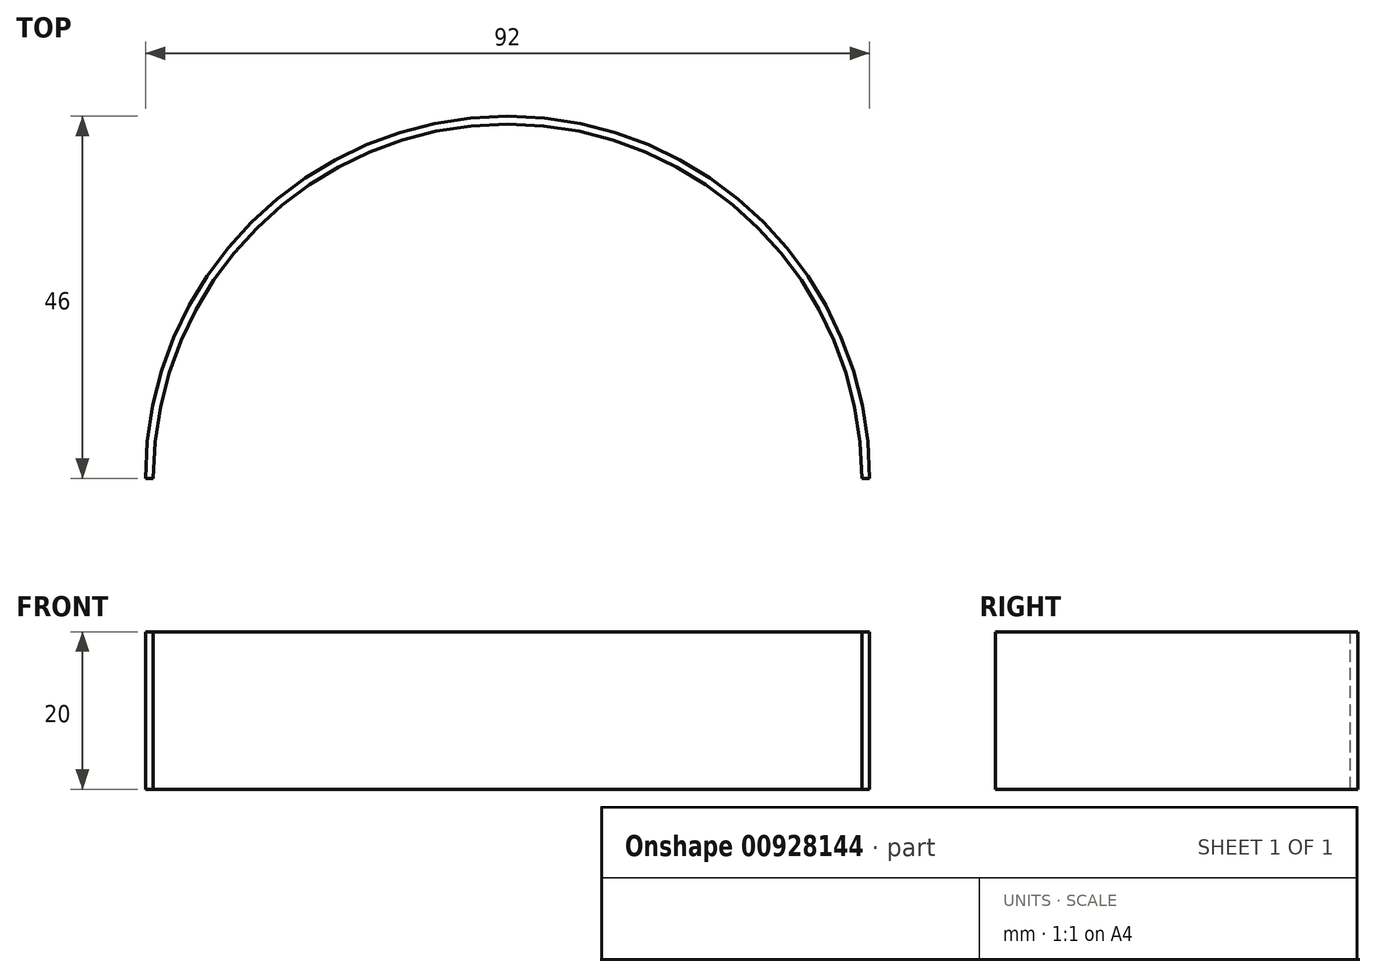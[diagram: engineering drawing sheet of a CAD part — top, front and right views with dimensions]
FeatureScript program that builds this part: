
annotation { "Feature Type Name" : "Feature", "Feature Type Description" : "" }
export const myFeature = defineFeature(function(context is Context, id is Id, definition is map)
    precondition{}
    {
        {
            var Q0;
            Q0=qCreatedBy(makeId("Top.planeOp"),FACE);
            var sketch = newSketch(context, id + "F0", { "sketchPlane" : qUnion([Q0])});
            skCircle(sketch, "E0", {"center": v(0, 0) * mm, "radius": 45 * mm});
            skCircle(sketch, "E1", {"center": v(0, 0) * mm, "radius": 46 * mm});
            skLineSegment(sketch, "E2", {"start": v(-64.55, 0) * mm, "end": v(65.08, 0) * mm});
            skSolve(sketch);
        }
        {
            var Q0;
            {var subQ0=sQuery(id+"F0.wireOp",EDGE,"E2");var subQ1=sQuery(id+"F0.wireOp",EDGE,"E0");var subQ2=makeQuery(id+"F0.imprint","INTERSECT",VERTEX,{"disambiguationData":[OD(0.0)],"derivedFrom":[subQ1,subQ0]});Q0=makeQuery(id+"F0.imprint","IMPRINT",FACE,{"disambiguationData":[TD([[makeQuery(id+"F0.imprint","IMPRINT",EDGE,{"disambiguationData":[TD([[subQ2,1.0]])],"derivedFrom":subQ1}),-1.0]])]});}
            extrude(context, id + "F1", {"entities" : qUnion([Q0]), "depth" : 20 * mm, "offsetDistance" : 25 * mm});
        }
    });
